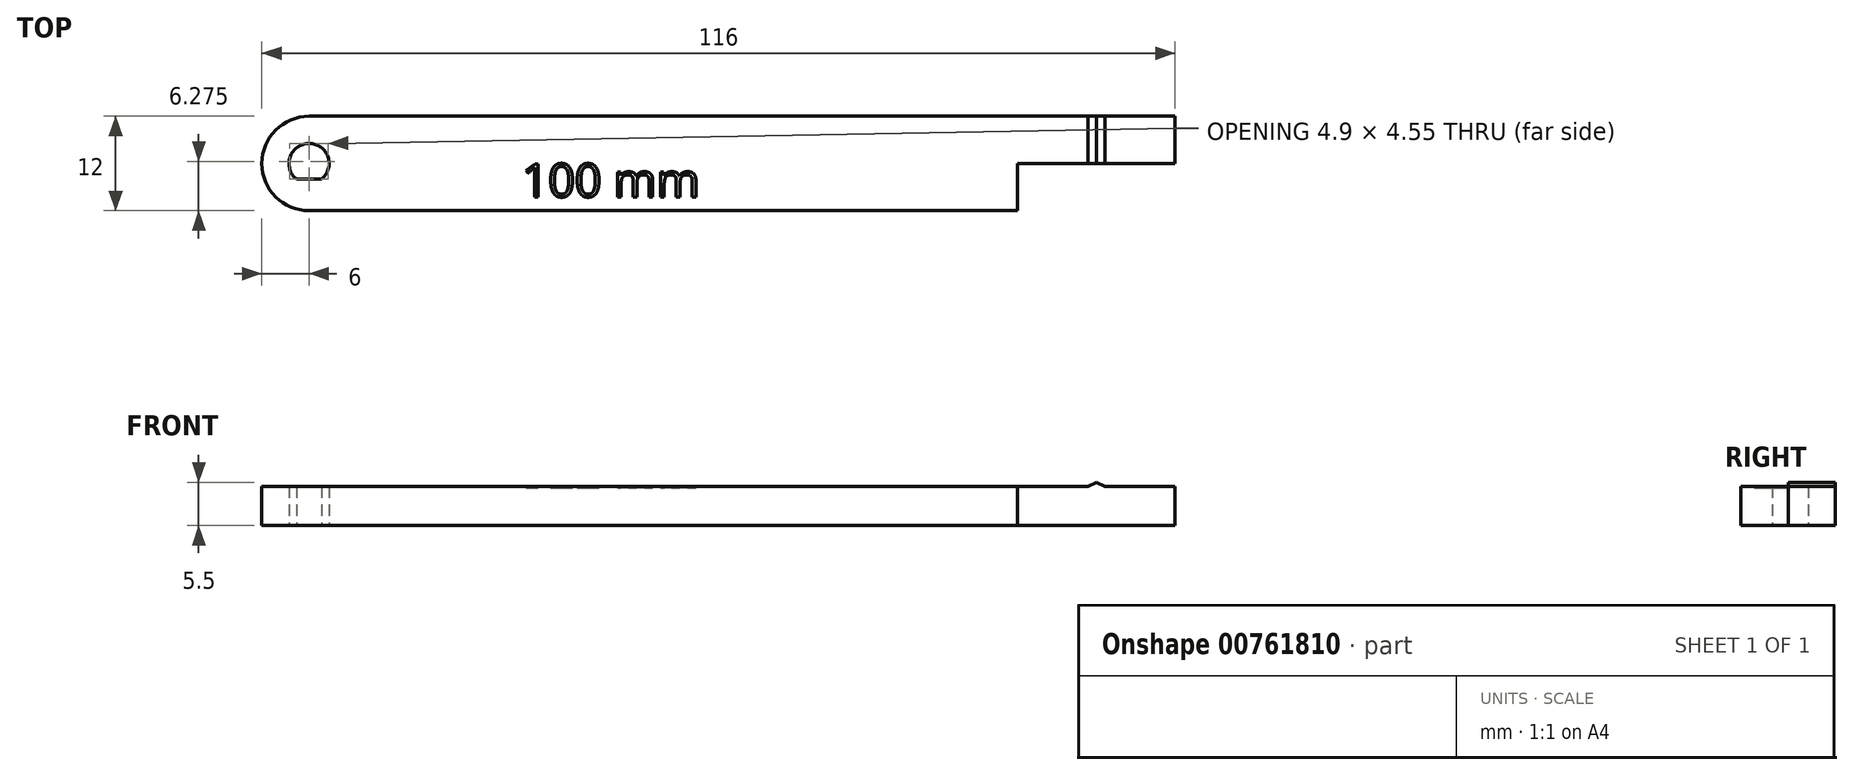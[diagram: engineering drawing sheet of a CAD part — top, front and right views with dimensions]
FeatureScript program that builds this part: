
annotation { "Feature Type Name" : "Feature", "Feature Type Description" : "" }
export const myFeature = defineFeature(function(context is Context, id is Id, definition is map)
    precondition{}
    {
        {
            var Q0;
            Q0=qCreatedBy(makeId("Top.planeOp"),FACE);
            var sketch = newSketch(context, id + "F0", { "sketchPlane" : qUnion([Q0])});
            skArc(sketch, "E0", {"start": v(1.58, -2) * mm, "mid": v(0, 2.55) * mm, "end": v(-1.58, -2) * mm});
            skLineSegment(sketch, "E1", {"start": v(0, -6) * mm, "end": v(90, -6) * mm});
            skLineSegment(sketch, "E2", {"start": v(90, -6) * mm, "end": v(90, 0) * mm});
            skLineSegment(sketch, "E3", {"start": v(90, 0) * mm, "end": v(110, 0) * mm});
            skLineSegment(sketch, "E4", {"start": v(110, 0) * mm, "end": v(110, 6) * mm});
            skLineSegment(sketch, "E5", {"start": v(110, 6) * mm, "end": v(0, 6) * mm});
            skArc(sketch, "E6", {"start": v(0, 6) * mm, "mid": v(-6, 0) * mm, "end": v(0, -6) * mm});
            skLineSegment(sketch, "E7", {"start": v(-1.58, -2) * mm, "end": v(1.58, -2) * mm});
            skSolve(sketch);
        }
        {
            var Q0;
            Q0 = qSketchRegion(id + "F0", true);
            extrude(context, id + "F1", {"entities" : qUnion([Q0]), "depth" : 5 * mm, "offsetDistance" : 25 * mm});
        }
        {
            var Q0;
            Q0=makeQuery(id+"F1.opExtrude","SWEPT_FACE",FACE,{"disambiguationData":[OSD([sQuery(id+"F0.wireOp",EDGE,"E3")])]});
            var sketch = newSketch(context, id + "F2", { "sketchPlane" : qUnion([Q0])});
            skLineSegment(sketch, "E8", {"start": v(98.93, 5) * mm, "end": v(100, 5.5) * mm});
            skPoint(sketch, "E8.endSnap0", {"position": v(100, 5) * mm});
            skLineSegment(sketch, "E9", {"start": v(100, 5.5) * mm, "end": v(101.07, 5) * mm});
            skLineSegment(sketch, "E10", {"start": v(101.07, 5) * mm, "end": v(98.93, 5) * mm});
            skSolve(sketch);
        }
        {
            var Q0;
            Q0 = qSketchRegion(id + "F2", true);
            var Q1;
            Q1=makeQuery(id+"F1.opExtrude","SWEPT_FACE",FACE,{"disambiguationData":[OSD([sQuery(id+"F0.wireOp",EDGE,"E5")])]});
            extrude(context, id + "F3", {"entities" : qUnion([Q0]), "operationType" : NewBodyOperationType.ADD, "oppositeDirection" : true, "depth" : 6 * mm, "endBoundEntityFace" : qUnion([Q1]), "offsetDistance" : 25 * mm});
        }
        {
            var Q0;
            {var subQ0=sQuery(id+"F0.wireOp",EDGE,"E2");var subQ1=sQuery(id+"F0.wireOp",EDGE,"E1");var subQ5=sQuery(id+"F0.wireOp",EDGE,"E3");var subQ6=sQuery(id+"F0.wireOp",EDGE,"E0");var subQ7=sQuery(id+"F0.wireOp",EDGE,"E5");var subQ8=sQuery(id+"F0.wireOp",EDGE,"E6");var subQ9=sQuery(id+"F0.wireOp",EDGE,"E7");Q0=makeQuery(id+"F3.boolean.opBoolean","SPLIT",FACE,{"disambiguationData":[TD([makeQuery(id+"F1.opExtrude","SWEPT_FACE",FACE,{"disambiguationData":[OSD([subQ6])]})])],"derivedFrom":makeQuery(id+"F1.opExtrude","CAP_FACE",FACE,{"disambiguationData":[OSD([subQ6,subQ1,subQ0,subQ5,sQuery(id+"F0.wireOp",EDGE,"E4"),subQ7,subQ8,subQ9])],"isStart":false})});}
            var sketch = newSketch(context, id + "F4", { "sketchPlane" : qUnion([Q0])});
            skText(sketch, "E11", { "text": "100 mm", "fontName": "OpenSans-Regular.ttf"});
            const initialGuessF4  = {"E11": [0.02703, -0.00424, 1, 0, 0.00424]};
            skSetInitialGuess(sketch, initialGuessF4);
            skSolve(sketch);
        }
        {
            var Q0;
            Q0 = qSketchRegion(id + "F4", true);
            extrude(context, id + "F5", {"entities" : qUnion([Q0]), "operationType" : NewBodyOperationType.REMOVE, "oppositeDirection" : true, "depth" : 0.2 * mm, "offsetDistance" : 25 * mm});
        }
    });
